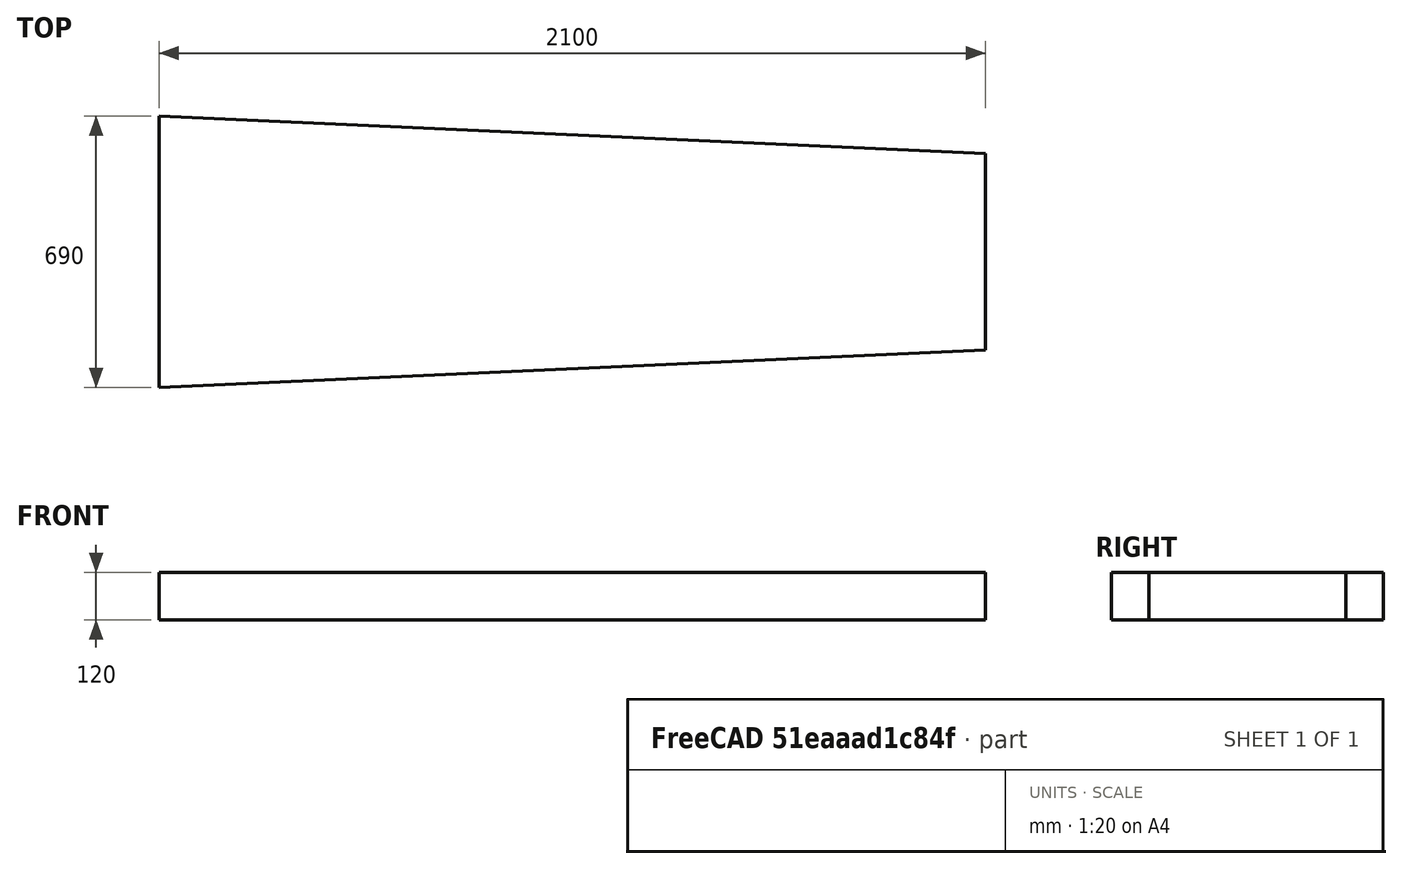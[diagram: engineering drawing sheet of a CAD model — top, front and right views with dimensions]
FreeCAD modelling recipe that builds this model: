
FCSTD DOCUMENT  (FreeCAD 0.18.3R)
Label: tent cat curvve
License: All rights reserved
LicenseURL: http://en.wikipedia.org/wiki/All_rights_reserved
objects: Sketcher::SketchObject×16, Part::Feature×16, PartDesign::Plane×5, App::DocumentObjectGroup×5, Part::Compound×4, Surface::Filling×2, PartDesign::Pad×1, PartDesign::Body×1
note: 46 computed .brp shape members not serialized (recipe doc carries the construction recipe); baked Part::Feature solids carry a one-line shape summary decoded from their .brp

FEATURE [Sketcher::SketchObject] Sketch
  MapMode = 5
  Support = -> [XY_Plane]
  sketch-geometry (4):
    g0: LineSegment StartX=-966.475 StartY=314.034 StartZ=0 EndX=1133.52 EndY=219.034 EndZ=0
    g1: LineSegment StartX=1133.52 StartY=219.034 StartZ=0 EndX=1133.52 EndY=-280.966 EndZ=0
    g2: LineSegment StartX=1133.52 StartY=-280.966 StartZ=0 EndX=-966.475 EndY=-375.966 EndZ=0
    g3: LineSegment StartX=-966.475 StartY=-375.966 StartZ=0 EndX=-966.475 EndY=314.034 EndZ=0
  constraints (10):
    c: Coincident(g0,g1)
    c: Coincident(g1,g2)
    c: Coincident(g2,g3)
    c: Coincident(g3,g0)
    c: Vertical(g1)
    c: Vertical(g3)
    c: Equal(g0,g2)
    c: DistanceX(g0,g0) = 2100
    c: DistanceY(g3,g3) = 690
    c: DistanceY(g1,g1) = 500
FEATURE [PartDesign::Pad] Pad  label="bathtub"
  Length = 120
  Length2 = 100
  Profile = -> Sketch
  Type = 0
FEATURE [PartDesign::Plane] DatumPlane
  AttachmentOffset = pos=(0,0,0) rot=(0,1,0;1.5708rad)
  Length = 1001
  MapMode = 45
  Placement = pos=(83.5246,-30.966,60) rot=(-0.57735,0.57735,0.57735;2.0944rad)
  ResizeMode = 0
  Support = -> [Pad]
  Width = 2351
FEATURE [Sketcher::SketchObject] Sketch001  label="construction sketch"
  ExternalGeometry = -> [Pad]
  MapMode = 5
  Placement = pos=(83.5246,-30.966,60) rot=(-0.57735,0.57735,0.57735;2.0944rad)
  Support = -> [DatumPlane]
  sketch-geometry (2):
    g0: LineSegment StartX=-60 StartY=-1050 StartZ=0 EndX=-60 EndY=1050 EndZ=0
    g1: LineSegment StartX=-60 StartY=680 StartZ=0 EndX=-680 EndY=680 EndZ=0
  constraints (6):
    c: Coincident(g0,g-4)
    c: Coincident(g0,g-3)
    c: PointOnObject(g1,g0)
    c: Horizontal(g1)
    c: DistanceX(g1,g1) = 620
    c: DistanceY(g1,g0) = 370
FEATURE [Sketcher::SketchObject] Sketch002  label="right low head triangle"
  ExternalGeometry = -> [Pad,Sketch001]
  MapMode = 5
  Placement = pos=(14.9994,-331.566,0) rot=(0.999489,0.022596,0.022596;1.57131rad)
  Support = -> [Pad]
  sketch-geometry (3):
    g0: LineSegment StartX=-982.479 StartY=120 StartZ=0 EndX=-597.265 EndY=300 EndZ=0
    g1: LineSegment StartX=-597.265 StartY=300 StartZ=0 EndX=-597.265 EndY=120 EndZ=0
    g2: LineSegment StartX=-982.479 StartY=120 StartZ=0 EndX=-597.265 EndY=120 EndZ=0
  constraints (7):
    c: PointOnObject(g0,g-4)
    c: Coincident(g1,g0)
    c: Coincident(g1,g-4)
    c: Coincident(g2,g1)
    c: DistanceY(g1,g1) = 180
    c: Coincident(g0,g2)
    c: Coincident(g0,g-3)
FEATURE [Sketcher::SketchObject] Sketch003  label="right rectangle"
  ExternalGeometry = -> [Sketch002,Pad]
  MapMode = 5
  Placement = pos=(14.9994,-331.566,0) rot=(0.999489,0.022596,0.022596;1.57131rad)
  Support = -> [Pad]
  sketch-geometry (4):
    g0: LineSegment StartX=-597.265 StartY=300 StartZ=0 EndX=-597.265 EndY=120 EndZ=0
    g1: LineSegment StartX=-597.265 StartY=120 StartZ=0 EndX=1119.67 EndY=120 EndZ=0
    g2: LineSegment StartX=-597.265 StartY=300 StartZ=0 EndX=1119.67 EndY=300 EndZ=0
    g3: LineSegment StartX=1119.67 StartY=120 StartZ=0 EndX=1119.67 EndY=300 EndZ=0
  constraints (9):
    c: Coincident(g0,g-3)
    c: Coincident(g0,g-3)
    c: Coincident(g1,g0)
    c: Coincident(g1,g-4)
    c: Coincident(g2,g0)
    c: Horizontal(g2)
    c: Coincident(g3,g1)
    c: Coincident(g3,g2)
    c: Vertical(g3)
FEATURE [Sketcher::SketchObject] Sketch004  label="left low head triangle"
  ExternalGeometry = -> [Sketch001,Pad]
  MapMode = 5
  Placement = pos=(12.2034,269.76,0) rot=(0.015984,0.707016,0.707016;3.10963rad)
  Support = -> [Pad]
  sketch-geometry (3):
    g0: LineSegment StartX=594.467 StartY=300 StartZ=0 EndX=979.68 EndY=120 EndZ=0
    g1: LineSegment StartX=594.467 StartY=120 StartZ=0 EndX=594.467 EndY=300 EndZ=0
    g2: LineSegment StartX=594.467 StartY=120 StartZ=0 EndX=979.68 EndY=120 EndZ=0
  constraints (7):
    c: PointOnObject(g0,g-3)
    c: Coincident(g0,g-4)
    c: Coincident(g1,g-3)
    c: Coincident(g1,g0)
    c: Coincident(g2,g1)
    c: Coincident(g2,g0)
    c: DistanceY(g1,g1) = 180
FEATURE [Sketcher::SketchObject] Sketch005  label="left rectangle"
  ExternalGeometry = -> [Pad,Sketch004]
  MapMode = 5
  Placement = pos=(12.2034,269.76,0) rot=(0.015984,0.707016,0.707016;3.10963rad)
  Support = -> [Pad]
  sketch-geometry (4):
    g0: LineSegment StartX=-1122.47 StartY=120 StartZ=0 EndX=594.467 EndY=120 EndZ=0
    g1: LineSegment StartX=594.467 StartY=120 StartZ=0 EndX=594.467 EndY=300 EndZ=0
    g2: LineSegment StartX=594.467 StartY=300 StartZ=0 EndX=-1122.47 EndY=300 EndZ=0
    g3: LineSegment StartX=-1122.47 StartY=300 StartZ=0 EndX=-1122.47 EndY=120 EndZ=0
  constraints (9):
    c: Coincident(g0,g-3)
    c: Coincident(g0,g-4)
    c: Coincident(g1,g0)
    c: Coincident(g1,g-4)
    c: Coincident(g2,g1)
    c: Horizontal(g2)
    c: Coincident(g3,g2)
    c: Coincident(g3,g0)
    c: Vertical(g3)
FEATURE [PartDesign::Plane] DatumPlane003
  Length = 1146.56
  MapMode = 13
  Placement = pos=(-843.142,-30.966,326.667) rot=(0.442712,-0.442712,-0.779752;1.81705rad)
  ResizeMode = 0
  Support = -> [Pad,Sketch001]
  Width = 1968.77
FEATURE [Sketcher::SketchObject] Sketch008  label="head big triangle"
  ExternalGeometry = -> [Pad,Sketch001]
  MapMode = 5
  Placement = pos=(-843.142,-30.966,326.667) rot=(0.442712,-0.442712,-0.779752;1.81705rad)
  Support = -> [DatumPlane003]
  sketch-geometry (3):
    g0: LineSegment StartX=0 StartY=481.341 StartZ=0 EndX=-345 EndY=-240.67 EndZ=0
    g1: LineSegment StartX=-345 StartY=-240.67 StartZ=0 EndX=345 EndY=-240.67 EndZ=0
    g2: LineSegment StartX=345 StartY=-240.67 StartZ=0 EndX=0 EndY=481.341 EndZ=0
  constraints (6):
    c: Coincident(g0,g-5)
    c: Coincident(g0,g-4)
    c: Coincident(g1,g0)
    c: Coincident(g1,g-3)
    c: Coincident(g2,g1)
    c: Coincident(g2,g0)
FEATURE [PartDesign::Plane] DatumPlane004  label="left high head triangle plane"
  Length = 2632.36
  MapMode = 13
  Placement = pos=(-714.869,193.231,386.667) rot=(-0.067097,0.459634,0.88557;3.39872rad)
  ResizeMode = 0
  Support = -> [Sketch004,Sketch001]
  Width = 1817.41
FEATURE [Sketcher::SketchObject] Sketch009  label="left high head triangle"
  ExternalGeometry = -> [Sketch004,Sketch001]
  MapMode = 5
  Placement = pos=(-714.869,193.231,386.667) rot=(-0.067097,0.459634,0.88557;3.39872rad)
  Support = -> [DatumPlane004]
  sketch-geometry (3):
    g0: LineSegment StartX=-157.211 StartY=-105.981 StartZ=0 EndX=-49.3624 EndY=432.075 EndZ=0
    g1: LineSegment StartX=-49.3624 StartY=432.075 StartZ=0 EndX=206.573 EndY=-326.095 EndZ=0
    g2: LineSegment StartX=206.573 StartY=-326.095 StartZ=0 EndX=-157.211 EndY=-105.981 EndZ=0
  constraints (6):
    c: Coincident(g0,g-3)
    c: Coincident(g0,g-5)
    c: Coincident(g1,g-5)
    c: Coincident(g1,g-4)
    c: Coincident(g2,g-4)
    c: Coincident(g0,g2)
FEATURE [PartDesign::Plane] DatumPlane005  label="right high head triangle plane"
  Length = 2632.36
  MapMode = 13
  Placement = pos=(-714.869,-255.163,386.667) rot=(0.953283,-0.139159,-0.268116;0.997163rad)
  ResizeMode = 0
  Support = -> [Sketch001,Sketch002]
  Width = 1817.41
FEATURE [Sketcher::SketchObject] Sketch010  label="right high head triangle"
  ExternalGeometry = -> [Sketch001,Sketch002]
  MapMode = 5
  Placement = pos=(-714.869,-255.163,386.667) rot=(0.953283,-0.139159,-0.268116;0.997163rad)
  Support = -> [DatumPlane005]
  sketch-geometry (3):
    g0: LineSegment StartX=49.3624 StartY=432.075 StartZ=0 EndX=157.211 EndY=-105.981 EndZ=0
    g1: LineSegment StartX=157.211 StartY=-105.981 StartZ=0 EndX=-206.573 EndY=-326.095 EndZ=0
    g2: LineSegment StartX=-206.573 StartY=-326.095 StartZ=0 EndX=49.3624 EndY=432.075 EndZ=0
  constraints (6):
    c: Coincident(g0,g-3)
    c: Coincident(g0,g-4)
    c: Coincident(g1,g0)
    c: Coincident(g2,g1)
    c: Coincident(g2,g0)
    c: Coincident(g1,g-5)
FEATURE [Sketcher::SketchObject] Sketch011  label="feet"
  ExternalGeometry = -> [Pad]
  MapMode = 5
  Placement = pos=(1133.52,0,0) rot=(0.57735,0.57735,0.57735;2.0944rad)
  Support = -> [Pad]
  sketch-geometry (6):
    g0: LineSegment [constr] StartX=-30.966 StartY=0 StartZ=0 EndX=-30.966 EndY=370 EndZ=0
    g1: LineSegment StartX=-280.966 StartY=300 StartZ=0 EndX=-30.966 EndY=370 EndZ=0
    g2: LineSegment StartX=-30.966 StartY=370 StartZ=0 EndX=219.034 EndY=300 EndZ=0
    g3: LineSegment StartX=-280.966 StartY=120 StartZ=0 EndX=219.034 EndY=120 EndZ=0
    g4: LineSegment StartX=219.034 StartY=120 StartZ=0 EndX=219.034 EndY=300 EndZ=0
    g5: LineSegment StartX=-280.966 StartY=120 StartZ=0 EndX=-280.966 EndY=300 EndZ=0
  constraints (15):
    c: Vertical(g0)
    c: Coincident(g1,g0)
    c: Coincident(g2,g1)
    c: Equal(g1,g2)
    c: DistanceY(g-3,g1) = 300
    c: DistanceY(g-3,g1) = 370
    c: Coincident(g3,g-4)
    c: Coincident(g3,g-4)
    c: Coincident(g4,g3)
    c: Coincident(g4,g2)
    c: Coincident(g1,g5)
    c: Vertical(g4)
    c: Vertical(g5)
    c: Coincident(g3,g5)
    c: Equal(g5,g4)
FEATURE [Part::Feature] Face001  label="D"
  shape: bbox 494.8 x 22.38 x 306.7 mm, 1 faces, 0 solids (baked)
FEATURE [Part::Feature] Face002
  shape: bbox 1887 x 85.35 x 198 mm, 1 faces, 0 solids (baked)
FEATURE [Part::Feature] Face  label="E"
  shape: bbox 494.8 x 22.38 x 306.7 mm, 1 faces, 0 solids (baked)
FEATURE [Part::Feature] Face003
  shape: bbox 1887 x 85.35 x 198 mm, 1 faces, 0 solids (baked)
FEATURE [Part::Feature] Face004  label="B"
  shape: bbox 407 x 759 x 682 mm, 1 faces, 0 solids (baked)
FEATURE [Part::Feature] Face008  label="A"
  shape: bbox 648.4 x 533.9 x 762.8 mm, 1 faces, 0 solids (baked)
FEATURE [Part::Feature] Face009  label="C"
  shape: bbox 648.4 x 533.9 x 762.8 mm, 1 faces, 0 solids (baked)
FEATURE [App::DocumentObjectGroup] Group  label="head triangle faces"
  Group = -> [Face004,Face001,Face,Face008,Face009]
FEATURE [Sketcher::SketchObject] Sketch013  label="pattern_head"
  sketch-geometry (15):
    g0: LineSegment StartX=2809.96 StartY=-4792.72 StartZ=0 EndX=3222.95 EndY=-4893.86 EndZ=0
    g1: LineSegment StartX=3187.72 StartY=-4717.34 StartZ=0 EndX=2809.96 EndY=-4792.72 EndZ=0
    g2: LineSegment StartX=3222.95 StartY=-4893.86 StartZ=0 EndX=3187.72 EndY=-4717.34 EndZ=0
    g3: LineSegment StartX=2809.96 StartY=-4792.72 StartZ=0 EndX=3222.97 EndY=-4893.86 EndZ=0
    g4: LineSegment StartX=3281.09 StartY=-5439.53 StartZ=0 EndX=3222.97 EndY=-4893.86 EndZ=0
    g5: LineSegment StartX=2809.96 StartY=-4792.72 StartZ=0 EndX=3281.09 EndY=-5439.53 EndZ=0
    g6: LineSegment StartX=2481.87 StartY=-5399.73 StartZ=0 EndX=2809.96 EndY=-4792.72 EndZ=0
    g7: LineSegment StartX=2809.96 StartY=-4792.72 StartZ=0 EndX=3281.09 EndY=-5439.53 EndZ=0
    g8: LineSegment StartX=3281.09 StartY=-5439.53 StartZ=0 EndX=2481.87 EndY=-5399.73 EndZ=0
    g9: LineSegment StartX=2792.73 StartY=-5689.84 StartZ=0 EndX=3281.09 EndY=-5439.53 EndZ=0
    g10: LineSegment StartX=2481.87 StartY=-5399.73 StartZ=0 EndX=2792.73 EndY=-5689.84 EndZ=0
    g11: LineSegment StartX=3281.09 StartY=-5439.53 StartZ=0 EndX=2481.87 EndY=-5399.73 EndZ=0
    g12: LineSegment StartX=2625.79 StartY=-5757.06 StartZ=0 EndX=2792.73 EndY=-5689.82 EndZ=0
    g13: LineSegment StartX=2481.87 StartY=-5399.73 StartZ=0 EndX=2625.79 EndY=-5757.06 EndZ=0
    g14: LineSegment StartX=2481.87 StartY=-5399.73 StartZ=0 EndX=2792.73 EndY=-5689.82 EndZ=0
  constraints (22):
    c: Coincident(g0,g1)
    c: Coincident(g1,g2)
    c: Coincident(g2,g0)
    c: Coincident(g3,g4)
    c: Coincident(g4,g5)
    c: Coincident(g5,g3)
    c: Coincident(g6,g7)
    c: Coincident(g7,g8)
    c: Coincident(g8,g6)
    c: Coincident(g9,g10)
    c: Coincident(g10,g11)
    c: Coincident(g11,g9)
    c: Coincident(g12,g13)
    c: Coincident(g13,g14)
    c: Coincident(g14,g12)
    c: Angle(g4,g5) = 0.523424
    c: Angle(g5,g0) = 0.701099
    c: Angle(g6,g5) = 1.12504
    c: Angle(g8,g6) = 1.12504
    c: Angle(g9,g10) = 1.91707
    c: Angle(g10,g12) = 1.13377
    c: Angle(g12,g13) = 1.5708
FEATURE [PartDesign::Plane] DatumPlane006  label="ridgeline plane"
  AttachmentOffset = pos=(0,0,0) rot=(1,0,0;1.5708rad)
  Length = 2532.41
  MapMode = 49
  Placement = pos=(-596.475,-30.966,740) rot=(0.989003,0.104578,-0.104578;1.58185rad)
  ResizeMode = 0
  Support = -> [Sketch001,Sketch011]
  Width = 1494.61
FEATURE [Part::Feature] Shell  label="flattened head triangle"
  shape: bbox 1127 x 1117 x 540 mm, 5 faces, 0 solids (baked)
FEATURE [Part::Feature] Face016
  Placement = pos=(8641,0,120) rot=(0,0,1;0rad)
  shape: bbox 2100 x 690 x 2e-07 mm, 1 faces, 0 solids (baked)
FEATURE [Part::Feature] Face017
  Placement = pos=(9894.52,0,-1013.52) rot=(0,-1,0;1.5708rad)
  shape: bbox 120 x 500 x 2e-07 mm, 1 faces, 0 solids (baked)
FEATURE [Part::Compound] Compound
  Links = -> [Face016,Face017]
FEATURE [Part::Feature] Face018
  Placement = pos=(8661.42,-451.443,-211.905) rot=(-0.998978,-0.045192,0;1.5708rad)
  shape: bbox 2105 x 214.9 x 2e-07 mm, 1 faces, 0 solids (baked)
FEATURE [Part::Compound] Compound001
  Links = -> [Compound,Face018]
FEATURE [Part::Feature] Face019
  Placement = pos=(8658.63,389.638,-150.036) rot=(0.998978,-0.045192,0;1.5708rad)
  shape: bbox 2105 x 214.9 x 2e-07 mm, 1 faces, 0 solids (baked)
FEATURE [Part::Compound] Compound002
  Links = -> [Compound001,Face019]
FEATURE [Part::Feature] Face020
  Placement = pos=(7554.52,0,-846.475) rot=(0,1,0;1.5708rad)
  shape: bbox 120 x 690 x 2e-07 mm, 1 faces, 0 solids (baked)
FEATURE [Sketcher::SketchObject] Sketch016  label="pattern_bathtub"
  Placement = pos=(-3000,-5000,0) rot=(0,0,1;0rad)
  sketch-geometry (20):
    g0: LineSegment StartX=7674.52 StartY=314.034 StartZ=0 EndX=9774.52 EndY=219.034 EndZ=0
    g1: LineSegment StartX=7674.52 StartY=-375.966 StartZ=0 EndX=7674.52 EndY=314.034 EndZ=0
    g2: LineSegment StartX=9774.52 StartY=-280.966 StartZ=0 EndX=7674.52 EndY=-375.966 EndZ=0
    g3: LineSegment StartX=9774.52 StartY=219.034 StartZ=0 EndX=9774.52 EndY=-280.966 EndZ=0
    g4: LineSegment StartX=9894.52 StartY=219.034 StartZ=0 EndX=9774.52 EndY=219.034 EndZ=0
    g5: LineSegment StartX=9774.52 StartY=219.034 StartZ=0 EndX=9774.52 EndY=-280.966 EndZ=0
    g6: LineSegment StartX=9894.52 StartY=-280.966 StartZ=0 EndX=9774.52 EndY=-280.966 EndZ=0
    g7: LineSegment StartX=9894.52 StartY=219.034 StartZ=0 EndX=9894.52 EndY=-280.966 EndZ=0
    g8: LineSegment StartX=9779.95 StartY=-400.843 StartZ=0 EndX=9774.52 EndY=-280.966 EndZ=0
    g9: LineSegment StartX=9774.52 StartY=-280.966 StartZ=0 EndX=7674.52 EndY=-375.966 EndZ=0
    g10: LineSegment StartX=7679.95 StartY=-495.843 StartZ=0 EndX=7674.52 EndY=-375.966 EndZ=0
    g11: LineSegment StartX=9779.95 StartY=-400.843 StartZ=0 EndX=7679.95 EndY=-495.843 EndZ=0
    g12: LineSegment StartX=7679.95 StartY=433.911 StartZ=0 EndX=7674.52 EndY=314.034 EndZ=0
    g13: LineSegment StartX=7674.52 StartY=314.034 StartZ=0 EndX=9774.52 EndY=219.034 EndZ=0
    g14: LineSegment StartX=9779.95 StartY=338.911 StartZ=0 EndX=9774.52 EndY=219.034 EndZ=0
    g15: LineSegment StartX=7679.95 StartY=433.911 StartZ=0 EndX=9779.95 EndY=338.911 EndZ=0
    g16: LineSegment StartX=7554.52 StartY=-375.966 StartZ=0 EndX=7674.52 EndY=-375.966 EndZ=0
    g17: LineSegment StartX=7674.52 StartY=-375.966 StartZ=0 EndX=7674.52 EndY=314.034 EndZ=0
    g18: LineSegment StartX=7554.52 StartY=314.034 StartZ=0 EndX=7674.52 EndY=314.034 EndZ=0
    g19: LineSegment StartX=7554.52 StartY=-375.966 StartZ=0 EndX=7554.52 EndY=314.034 EndZ=0
  constraints (30):
    c: Coincident(g0,g1)
    c: Vertical(g1)
    c: Coincident(g1,g2)
    c: Coincident(g2,g3)
    c: Vertical(g3)
    c: Coincident(g3,g0)
    c: Horizontal(g4)
    c: Coincident(g4,g5)
    c: Vertical(g5)
    c: Coincident(g5,g6)
    c: Horizontal(g6)
    c: Coincident(g6,g7)
    c: Vertical(g7)
    c: Coincident(g7,g4)
    c: Coincident(g8,g9)
    c: Coincident(g9,g10)
    c: Coincident(g10,g11)
    c: Coincident(g11,g8)
    c: Coincident(g12,g13)
    c: Coincident(g13,g14)
    c: Coincident(g14,g15)
    c: Coincident(g15,g12)
    c: Horizontal(g16)
    c: Coincident(g16,g17)
    c: Vertical(g17)
    c: Coincident(g17,g18)
    c: Horizontal(g18)
    c: Coincident(g18,g19)
    c: Vertical(g19)
    c: Coincident(g19,g16)
FEATURE [Sketcher::SketchObject] Sketch014
  ExternalGeometry = -> [Sketch001,Sketch011]
  MapMode = 5
  Placement = pos=(-596.475,-30.966,740) rot=(0.989003,0.104578,-0.104578;1.58185rad)
  Support = -> [DatumPlane006]
  sketch-geometry (6):
    g0: ArcOfHyperbola CenterX=884.562 CenterY=-79.0092 CenterZ=0 NormalX=0 NormalY=0 NormalZ=1 MajorRadius=29.0092 MinorRadius=349.164 AngleXU=1.5708 StartAngle=-1.65955 EndAngle=1.65955
    g1: LineSegment [constr] StartX=884.562 StartY=-50 StartZ=0 EndX=884.562 EndY=-108.018 EndZ=0
    g2: LineSegment [constr] StartX=535.398 StartY=-50 StartZ=0 EndX=1233.73 EndY=-50 EndZ=0
    g3: GeomPoint X=884.562 Y=271.358 Z=0
    g4: LineSegment [constr] StartX=0 StartY=0 StartZ=0 EndX=1769.12 EndY=0 EndZ=0
    g5: LineSegment [constr] StartX=884.562 StartY=0 StartZ=0 EndX=884.562 EndY=-50 EndZ=0
  constraints (11):
    c: InternalAlignment(g1,g0)
    c: InternalAlignment(g2,g0)
    c: InternalAlignment(g3,g0)
    c: Coincident(g0,g-4)
    c: Coincident(g0,g-1)
    c: Coincident(g4,g0)
    c: Coincident(g4,g0)
    c: Coincident(g5,g1)
    c: Perpendicular(g4,g5)
    c: Symmetric(g0,g0,g5)
    c: Distance(g5) = 50
FEATURE [PartDesign::Body] Body  label="tent construction"
  Group = -> [Sketch,Pad,DatumPlane,Sketch001,Sketch002,Sketch003,Sketch004,Sketch005,DatumPlane003,Sketch008,DatumPlane004,Sketch009,DatumPlane005,Sketch010,Sketch011,DatumPlane006,Sketch014]
  Origin = -> Origin
  Tip = -> Pad
FEATURE [Part::Feature] Face021  label="feet001"
  shape: bbox 2e-07 x 550 x 275 mm, 1 faces, 0 solids (baked)
FEATURE [Sketcher::SketchObject] Sketch017  label="pattern_feet"
  Placement = pos=(4000,-5000,0) rot=(0,0,1;0rad)
  sketch-geometry (5):
    g0: LineSegment StartX=-300 StartY=-280.966 StartZ=0 EndX=-370 EndY=-30.966 EndZ=0
    g1: LineSegment StartX=-120 StartY=-280.966 StartZ=0 EndX=-300 EndY=-280.966 EndZ=0
    g2: LineSegment StartX=-120 StartY=219.034 StartZ=0 EndX=-120 EndY=-280.966 EndZ=0
    g3: LineSegment StartX=-300 StartY=219.034 StartZ=0 EndX=-120 EndY=219.034 EndZ=0
    g4: LineSegment StartX=-370 StartY=-30.966 StartZ=0 EndX=-300 EndY=219.034 EndZ=0
  constraints (5):
    c: Coincident(g0,g1)
    c: Coincident(g1,g2)
    c: Coincident(g2,g3)
    c: Coincident(g3,g4)
    c: Coincident(g4,g0)
FEATURE [Surface::Filling] Surface
  Anisotropy = false
  BoundaryEdges = -> [Sketch014,Sketch011,Sketch003,Sketch010]
  BoundaryOrder = [0,0,0,0]
  Degree = 3
  Iterations = 2
  MaximumDegree = 8
  MaximumSegments = 9
  PointsOnCurve = 15
  TolAngular = 0.01
  TolCurvature = 0.1
  Tolerance2d = 1e-05
  Tolerance3d = 0.0001
FEATURE [Surface::Filling] Surface001
  Anisotropy = false
  BoundaryEdges = -> [Sketch014,Sketch009,Sketch005,Sketch011]
  BoundaryOrder = [0,0,0,0]
  Degree = 3
  Iterations = 2
  MaximumDegree = 8
  MaximumSegments = 9
  PointsOnCurve = 15
  TolAngular = 0.01
  TolCurvature = 0.1
  Tolerance2d = 1e-05
  Tolerance3d = 0.0001
FEATURE [App::DocumentObjectGroup] Group001  label="sides and feet faces"
  Group = -> [Face002,Face003,Face021,Surface,Surface001]
FEATURE [App::DocumentObjectGroup] Group004  label="tent model"
  Group = -> [Body,Group,Group001]
FEATURE [Part::Feature] Shape002  label="mesh panel"
  Placement = pos=(2926,0,0) rot=(0,0,1;0rad)
  shape: bbox 1751 x 797.6 x 2e-07 mm, 0 faces, 0 solids (baked)
FEATURE [Sketcher::SketchObject] Sketch018  label="pattern_mesh"
  Placement = pos=(5000,-6000,0) rot=(0,0,1;0rad)
  sketch-geometry (27):
    g0: LineSegment StartX=-770.412 StartY=-89.4026 StartZ=0 EndX=-745.901 EndY=100.807 EndZ=0
    g1: LineSegment StartX=-745.901 StartY=100.807 StartZ=0 EndX=-722.727 EndY=285.517 EndZ=0
    g2: LineSegment StartX=-722.727 StartY=285.517 StartZ=0 EndX=-702.396 EndY=454.641 EndZ=0
    g3: LineSegment StartX=-702.396 StartY=454.641 StartZ=0 EndX=-527.653 EndY=385.415 EndZ=0
    g4: LineSegment StartX=-527.653 StartY=385.415 StartZ=0 EndX=-309.32 EndY=300.722 EndZ=0
    g5: LineSegment StartX=-309.32 StartY=300.722 StartZ=0 EndX=-59.6446 EndY=207.8 EndZ=0
    g6: LineSegment StartX=-59.6446 StartY=207.8 StartZ=0 EndX=164.743 EndY=132.298 EndZ=0
    g7: LineSegment StartX=164.743 StartY=132.298 StartZ=0 EndX=341.313 EndY=79.6577 EndZ=0
    g8: LineSegment StartX=341.313 StartY=79.6577 StartZ=0 EndX=530.105 EndY=27.7274 EndZ=0
    g9: LineSegment StartX=530.105 StartY=27.7274 StartZ=0 EndX=668.162 EndY=-9.06999 EndZ=0
    g10: LineSegment StartX=668.162 StartY=-9.06999 StartZ=0 EndX=783.541 EndY=-39.0305 EndZ=0
    g11: LineSegment StartX=783.541 StartY=-39.0305 StartZ=0 EndX=887.872 EndY=-65.566 EndZ=0
    g12: LineSegment StartX=887.872 StartY=-65.566 StartZ=0 EndX=980.582 EndY=-88.9749 EndZ=0
    g13: LineSegment StartX=980.582 StartY=-88.9749 StartZ=0 EndX=962.48 EndY=-172.569 EndZ=0
    g14: LineSegment StartX=962.48 StartY=-172.569 StartZ=0 EndX=945.053 EndY=-254.741 EndZ=0
    g15: LineSegment StartX=945.053 StartY=-254.741 StartZ=0 EndX=926.696 EndY=-342.926 EndZ=0
    g16: LineSegment StartX=926.696 StartY=-342.926 StartZ=0 EndX=835.927 EndY=-328.011 EndZ=0
    g17: LineSegment StartX=835.927 StartY=-328.011 StartZ=0 EndX=737.655 EndY=-311.787 EndZ=0
    g18: LineSegment StartX=737.655 StartY=-311.787 StartZ=0 EndX=628.819 EndY=-294.251 EndZ=0
    g19: LineSegment StartX=628.819 StartY=-294.251 StartZ=0 EndX=507.248 EndY=-274.668 EndZ=0
    g20: LineSegment StartX=507.248 StartY=-274.668 StartZ=0 EndX=372.962 EndY=-253.531 EndZ=0
    g21: LineSegment StartX=372.962 StartY=-253.531 StartZ=0 EndX=223.686 EndY=-230.138 EndZ=0
    g22: LineSegment StartX=223.686 StartY=-230.138 StartZ=0 EndX=58.3506 EndY=-204.705 EndZ=0
    g23: LineSegment StartX=58.3506 StartY=-204.705 StartZ=0 EndX=-133.925 EndY=-175.273 EndZ=0
    g24: LineSegment StartX=-133.925 StartY=-175.273 StartZ=0 EndX=-367.461 EndY=-142.27 EndZ=0
    g25: LineSegment StartX=-367.461 StartY=-142.27 StartZ=0 EndX=-579.126 EndY=-114.093 EndZ=0
    g26: LineSegment StartX=-579.126 StartY=-114.093 StartZ=0 EndX=-770.412 EndY=-89.4026 EndZ=0
  constraints (27):
    c: Coincident(g0,g1)
    c: Coincident(g1,g2)
    c: Coincident(g2,g3)
    c: Coincident(g3,g4)
    c: Coincident(g4,g5)
    c: Coincident(g5,g6)
    c: Coincident(g6,g7)
    c: Coincident(g7,g8)
    c: Coincident(g8,g9)
    c: Coincident(g9,g10)
    c: Coincident(g10,g11)
    c: Coincident(g11,g12)
    c: Coincident(g12,g13)
    c: Coincident(g13,g14)
    c: Coincident(g14,g15)
    c: Coincident(g15,g16)
    c: Coincident(g16,g17)
    c: Coincident(g17,g18)
    c: Coincident(g18,g19)
    c: Coincident(g19,g20)
    c: Coincident(g20,g21)
    c: Coincident(g21,g22)
    c: Coincident(g22,g23)
    c: Coincident(g23,g24)
    c: Coincident(g24,g25)
    c: Coincident(g25,g26)
    c: Coincident(g26,g0)
FEATURE [Part::Feature] Sketch003001  label="right rectangle001"
  Placement = pos=(14.9994,-331.566,0) rot=(0.999489,0.022596,0.022596;1.57131rad)
  shape: bbox 1715 x 77.59 x 180 mm, 0 faces, 0 solids (baked)
FEATURE [Part::Compound] Compound003  label="flattened bathtub"
  Links = -> [Compound002,Face020,Sketch003001]
FEATURE [App::DocumentObjectGroup] Group002  label="pattern construction"
  Group = -> [Shell,Compound003,Shape002]
FEATURE [Sketcher::SketchObject] Sketch003002  label="pattern_sides"
  Placement = pos=(3976,-6781,0) rot=(0,0,1;0rad)
  sketch-geometry (4):
    g0: LineSegment StartX=-610.213 StartY=272.702 StartZ=0 EndX=-602.078 EndY=92.8859 EndZ=0
    g1: LineSegment StartX=-602.078 StartY=92.8859 StartZ=0 EndX=1113.1 EndY=170.477 EndZ=0
    g2: LineSegment StartX=1113.1 StartY=170.477 StartZ=0 EndX=1104.97 EndY=350.293 EndZ=0
    g3: LineSegment StartX=-610.213 StartY=272.702 StartZ=0 EndX=1104.97 EndY=350.293 EndZ=0
  constraints (4):
    c: Coincident(g0,g1)
    c: Coincident(g1,g2)
    c: Coincident(g2,g3)
    c: Coincident(g3,g0)
FEATURE [App::DocumentObjectGroup] Group003  label="pattern sketchs"
  Group = -> [Sketch013,Sketch016,Sketch017,Group002,Sketch018,Sketch003002]
